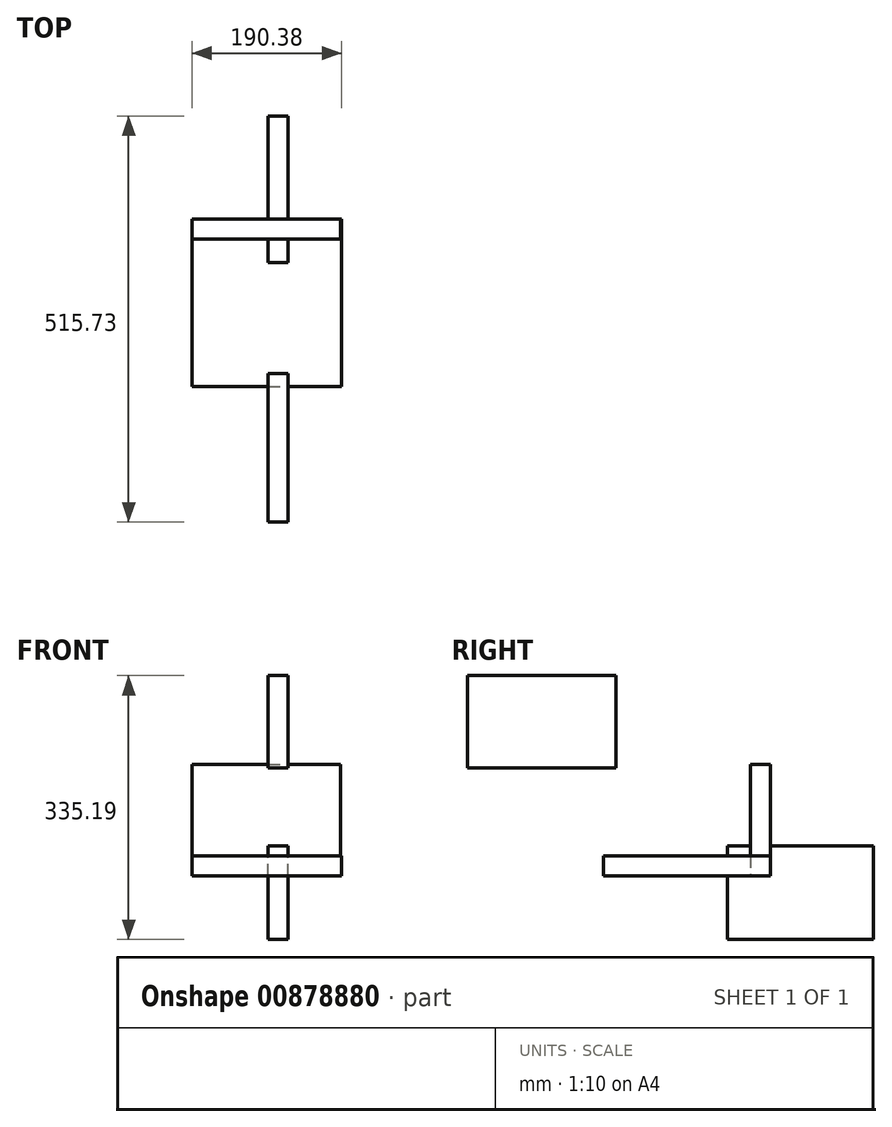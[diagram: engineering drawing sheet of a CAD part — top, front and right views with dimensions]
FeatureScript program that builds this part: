
annotation { "Feature Type Name" : "Feature", "Feature Type Description" : "" }
export const myFeature = defineFeature(function(context is Context, id is Id, definition is map)
    precondition{}
    {
        {
            var Q0;
            Q0=qCreatedBy(makeId("Top.planeOp"),FACE);
            var sketch = newSketch(context, id + "F0", { "sketchPlane" : qUnion([Q0])});
            skLineSegment(sketch, "E0.bottom", {"start": v(-96.5, -212.45) * mm, "end": v(93.31, -212.45) * mm});
            skLineSegment(sketch, "E0.top", {"start": v(-96.5, 0) * mm, "end": v(93.31, 0) * mm});
            skLineSegment(sketch, "E0.left", {"start": v(-96.5, -212.45) * mm, "end": v(-96.5, 0) * mm});
            skLineSegment(sketch, "E0.right", {"start": v(93.31, -212.45) * mm, "end": v(93.31, 0) * mm});
            skSolve(sketch);
        }
        {
            var Q0;
            Q0=qCreatedBy(makeId("Front.planeOp"),FACE);
            var sketch = newSketch(context, id + "F1", { "sketchPlane" : qUnion([Q0])});
            skLineSegment(sketch, "E1.bottom", {"start": v(-97.07, 141.46) * mm, "end": v(91.6, 141.46) * mm});
            skLineSegment(sketch, "E1.top", {"start": v(-97.07, 0) * mm, "end": v(91.6, 0) * mm});
            skLineSegment(sketch, "E1.left", {"start": v(-97.07, 141.46) * mm, "end": v(-97.07, 0) * mm});
            skLineSegment(sketch, "E1.right", {"start": v(91.6, 141.46) * mm, "end": v(91.6, 0) * mm});
            skSolve(sketch);
        }
        {
            var Q0;
            Q0=makeQuery(id+"F1.imprint","IMPRINT",FACE,{"disambiguationData":[TD([[makeQuery(id+"F1.imprint","IMPRINT",EDGE,{"derivedFrom":sQuery(id+"F1.wireOp",EDGE,"E1.bottom")}),-1.0]])]});
            extrude(context, id + "F2", {"entities" : qUnion([Q0]), "depth" : 25.4 * mm, "offsetDistance" : 25.4 * mm});
        }
        {
            var Q0;
            Q0=makeQuery(id+"F0.imprint","IMPRINT",FACE,{"disambiguationData":[TD([[makeQuery(id+"F0.imprint","IMPRINT",EDGE,{"derivedFrom":sQuery(id+"F0.wireOp",EDGE,"E0.bottom")}),1.0]])]});
            extrude(context, id + "F3", {"entities" : qUnion([Q0]), "operationType" : NewBodyOperationType.ADD, "depth" : 25.4 * mm, "offsetDistance" : 25.4 * mm});
        }
        {
            var Q0;
            Q0=qCreatedBy(makeId("Right.planeOp"),FACE);
            var sketch = newSketch(context, id + "F4", { "sketchPlane" : qUnion([Q0])});
            skLineSegment(sketch, "E2.bottom", {"start": v(-196.24, 254.49) * mm, "end": v(-384.73, 254.49) * mm});
            skLineSegment(sketch, "E2.top", {"start": v(-196.24, 137.13) * mm, "end": v(-384.73, 137.13) * mm});
            skLineSegment(sketch, "E2.left", {"start": v(-196.24, 254.49) * mm, "end": v(-196.24, 137.13) * mm});
            skLineSegment(sketch, "E2.right", {"start": v(-384.73, 254.49) * mm, "end": v(-384.73, 137.13) * mm});
            skSolve(sketch);
        }
        {
            var Q0;
            Q0=makeQuery(id+"F4.imprint","IMPRINT",FACE,{"disambiguationData":[TD([[makeQuery(id+"F4.imprint","IMPRINT",EDGE,{"derivedFrom":sQuery(id+"F4.wireOp",EDGE,"E2.bottom")}),1.0]])]});
            extrude(context, id + "F5", {"entities" : qUnion([Q0]), "depth" : 25.4 * mm, "offsetDistance" : 25.4 * mm});
        }
        {
            var Q0;
            Q0=qCreatedBy(makeId("Right.planeOp"),FACE);
            var sketch = newSketch(context, id + "F6", { "sketchPlane" : qUnion([Q0])});
            skLineSegment(sketch, "E3.bottom", {"start": v(131, 37.97) * mm, "end": v(-54.87, 37.97) * mm});
            skLineSegment(sketch, "E3.top", {"start": v(131, -80.7) * mm, "end": v(-54.87, -80.7) * mm});
            skLineSegment(sketch, "E3.left", {"start": v(131, 37.97) * mm, "end": v(131, -80.7) * mm});
            skLineSegment(sketch, "E3.right", {"start": v(-54.87, 37.97) * mm, "end": v(-54.87, -80.7) * mm});
            skSolve(sketch);
        }
        {
            var Q0;
            Q0=makeQuery(id+"F6.imprint","IMPRINT",FACE,{"disambiguationData":[TD([[makeQuery(id+"F6.imprint","IMPRINT",EDGE,{"derivedFrom":sQuery(id+"F6.wireOp",EDGE,"E3.bottom")}),1.0]])]});
            extrude(context, id + "F7", {"entities" : qUnion([Q0]), "operationType" : NewBodyOperationType.ADD, "depth" : 25.4 * mm, "offsetDistance" : 25.4 * mm});
        }
    });
